# Revit family: РИДАН_APT-R3_Автоматический балансировочный клапан(Ду32-40)
name_source: partatom
category: Арматура трубопроводов
units: mm (PartAtom-declared; Revit-internal decimal feet)

## family parameters
Всегда вертикально = Да
На основе рабочей плоскости = Нет
Общий = Нет
При загрузке вырезать с полостями = Нет
Размер круглого соединителя = Использовать диаметр
Тип детали = Вставляется

## types (2) — shared parameters
ADSK_Версия Revit = 2019
ADSK_Версия семейства = 1.0
ADSK_Единица измерения = шт.
ADSK_Завод-изготовитель = ООО «Ридан-Трейд»
ADSK_Количество = 1
LT = APT-R3_32_40
LT_Kv = APT-R3_Kv
URL = https://ridan.ru
a = 18 мм
g = 44 мм
i = 18 мм

## per-type parameters (varying)
| type | ADSK_Диаметр условный | ADSK_Код изделия | ADSK_Марка | ADSK_Масса | ADSK_Наименование | b | c | d | e | f | h | j | k | l | m |
| DN 32 | 32 мм | 003Z5704R3 | APT-R3 DN32 | 3.6 | Клапан балансировочный автоматический резьбовой, диапазон настройки 5-25 кПа, PN16, Tmax=120C, DN32 | 19 мм | 30 мм | 59 мм | 46 мм | 48 мм | 29 мм | 50 мм | 42 мм | 21 мм | 74 мм |
| DN 40 | 40 мм | 003Z5705R3 | APT-R3 DN40 | 3.8 | Клапан балансировочный автоматический резьбовой, диапазон настройки 5-25 кПа, PN16, Tmax=120C, DN40 | 18 мм | 32 мм | 64 мм | 50 мм | 54 мм | 34 мм | 55 мм | 48 мм | 25 мм | 70 мм |
